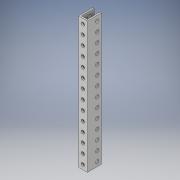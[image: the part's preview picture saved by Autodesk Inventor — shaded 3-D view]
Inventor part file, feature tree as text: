
AUTODESK INVENTOR PART (.ipt)
format: ipt  version: 2019 (Build 230136000, 136)  size: 198,656 bytes
history: native  units: in
note: dims shown in document units (in); Inventor stores cm internally (conversion verified against a paired STEP export)
features: extrude x1, sketch x1, fillet x1
ambient origin geometry x8: Origin, YZ Plane, XZ Plane, XY Plane, X Axis, Y Axis, Z Axis, Center Point
bodies: Solid1 (feature_tree)
feature tree (3):
  extrude  "Extrusion1"  [1 undecoded]
  sketch  "Sketch1"  dims[d0=1.0in d1=0.0in]
  fillet  "Fillet1"  [1 undecoded]
note: 2 required parameter values undecoded (feature->parameter linkage not recoverable at this tier; creation-order binding heuristic only, values carry confidence <= 0.55)
